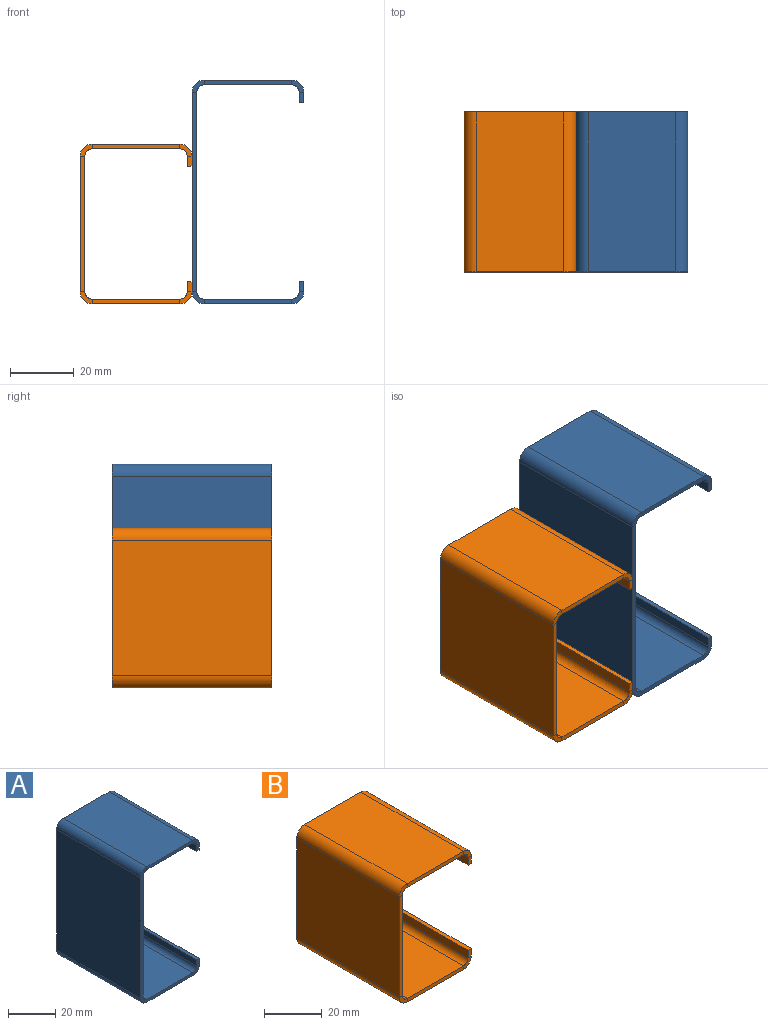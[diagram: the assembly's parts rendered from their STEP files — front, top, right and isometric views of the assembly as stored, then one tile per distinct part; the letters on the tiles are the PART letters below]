
ASSEMBLY  parts=2 mates=1
PART A: 38 faces, bbox 35x50x70 mm
  f0: plane 27.4x1.5mm, normal (0,1,0), area 41.1mm2, adj f2,f3,f26,f35
  f1: plane 27.4x1.5mm, normal (0,-1,0), area 41.1mm2, adj f2,f3,f25,f34
  f2: plane 50x27.4mm, normal (0,0,1), area 1370mm2, adj f0,f1,f28,f37
  f3: plane 50x27.4mm, normal (0,0,-1), area 1370mm2, adj f0,f1,f27,f36
  f4: plane 62.4x1.5mm, normal (0,1,0), area 93.6mm2, adj f6,f7,f22,f26
  f5: plane 62.4x1.5mm, normal (0,-1,0), area 93.6mm2, adj f6,f7,f21,f25
  f6: plane 62.4x50mm, normal (1,0,0), area 3120mm2, adj f4,f5,f24,f28
  f7: plane 62.4x50mm, normal (-1,0,0), area 3120mm2, adj f4,f5,f23,f27
  f8: plane 27.4x1.5mm, normal (0,1,0), area 41.1mm2, adj f10,f11,f18,f22
  f9: plane 27.4x1.5mm, normal (0,-1,0), area 41.1mm2, adj f10,f11,f17,f21
  f10: plane 50x27.4mm, normal (0,0,-1), area 1370mm2, adj f8,f9,f20,f24
  f11: plane 50x27.4mm, normal (0,0,1), area 1370mm2, adj f8,f9,f19,f23
  f12: plane 3.2x1.5mm, normal (0,1,0), area 4.8mm2, adj f13,f15,f16,f18
  f13: plane 50x1.5mm, normal (0,0,-1), area 75mm2, adj f12,f14,f15,f16
  f14: plane 3.2x1.5mm, normal (0,-1,0), area 4.8mm2, adj f13,f15,f16,f17
  f15: plane 50x3.2mm, normal (-1,0,0), area 160mm2, adj f12,f13,f14,f20
  f16: plane 50x3.2mm, normal (1,0,0), area 160mm2, adj f12,f13,f14,f19
  f17: plane 3.8x3.8mm, normal (0,-1,0), area 7.2mm2, adj f9,f14,f19,f20
  f18: plane 3.8x3.8mm, normal (0,1,0), area 7.2mm2, adj f8,f12,f19,f20
  f19: cylinder r=3.8mm len=50mm, axis (0,-1,0), area 298.5mm2, adj f11,f16,f17,f18
  f20: cylinder r=2.3mm len=50mm, axis (0,-1,0), area 180.6mm2, adj f10,f15,f17,f18
  f21: plane 3.8x3.8mm, normal (0,-1,0), area 7.2mm2, adj f5,f9,f23,f24
  f22: plane 3.8x3.8mm, normal (0,1,0), area 7.2mm2, adj f4,f8,f23,f24
  f23: cylinder r=3.8mm len=50mm, axis (0,-1,0), area 298.5mm2, adj f7,f11,f21,f22
  f24: cylinder r=2.3mm len=50mm, axis (0,-1,0), area 180.6mm2, adj f6,f10,f21,f22
  f25: plane 3.8x3.8mm, normal (0,-1,0), area 7.2mm2, adj f1,f5,f27,f28
  f26: plane 3.8x3.8mm, normal (0,1,0), area 7.2mm2, adj f0,f4,f27,f28
  f27: cylinder r=3.8mm len=50mm, axis (0,-1,0), area 298.5mm2, adj f3,f7,f25,f26
  f28: cylinder r=2.3mm len=50mm, axis (0,-1,0), area 180.6mm2, adj f2,f6,f25,f26
  f29: plane 3.2x1.5mm, normal (0,1,0), area 4.8mm2, adj f31,f32,f33,f35
  f30: plane 3.2x1.5mm, normal (0,-1,0), area 4.8mm2, adj f31,f32,f33,f34
  f31: plane 50x1.5mm, normal (0,0,1), area 75mm2, adj f29,f30,f32,f33
  f32: plane 50x3.2mm, normal (-1,0,0), area 160mm2, adj f29,f30,f31,f37
  f33: plane 50x3.2mm, normal (1,0,0), area 160mm2, adj f29,f30,f31,f36
  f34: plane 3.8x3.8mm, normal (0,-1,0), area 7.2mm2, adj f1,f30,f36,f37
  f35: plane 3.8x3.8mm, normal (0,1,0), area 7.2mm2, adj f0,f29,f36,f37
  f36: cylinder r=3.8mm len=50mm, axis (0,-1,0), area 298.5mm2, adj f3,f33,f34,f35
  f37: cylinder r=2.3mm len=50mm, axis (0,-1,0), area 180.6mm2, adj f2,f32,f34,f35
PART B: 38 faces, bbox 35x50x50 mm
  f0: plane 3.2x1.5mm, normal (0,1,0), area 4.8mm2, adj f2,f3,f4,f35
  f1: plane 3.2x1.5mm, normal (0,-1,0), area 4.8mm2, adj f2,f3,f4,f34
  f2: plane 50x1.5mm, normal (0,0,-1), area 75mm2, adj f0,f1,f3,f4
  f3: plane 50x3.2mm, normal (1,0,0), area 160mm2, adj f0,f1,f2,f36
  f4: plane 50x3.2mm, normal (-1,0,0), area 160mm2, adj f0,f1,f2,f37
  f5: plane 27.4x1.5mm, normal (0,1,0), area 41.1mm2, adj f7,f8,f31,f35
  f6: plane 27.4x1.5mm, normal (0,-1,0), area 41.1mm2, adj f7,f8,f30,f34
  f7: plane 50x27.4mm, normal (0,0,1), area 1370mm2, adj f5,f6,f32,f36
  f8: plane 50x27.4mm, normal (0,0,-1), area 1370mm2, adj f5,f6,f33,f37
  f9: plane 42.4x1.5mm, normal (0,1,0), area 63.6mm2, adj f11,f12,f27,f31
  f10: plane 42.4x1.5mm, normal (0,-1,0), area 63.6mm2, adj f11,f12,f26,f30
  f11: plane 50x42.4mm, normal (-1,0,0), area 2120mm2, adj f9,f10,f28,f32
  f12: plane 50x42.4mm, normal (1,0,0), area 2120mm2, adj f9,f10,f29,f33
  f13: plane 27.4x1.5mm, normal (0,1,0), area 41.1mm2, adj f15,f16,f23,f27
  f14: plane 27.4x1.5mm, normal (0,-1,0), area 41.1mm2, adj f15,f16,f22,f26
  f15: plane 50x27.4mm, normal (0,0,-1), area 1370mm2, adj f13,f14,f24,f28
  f16: plane 50x27.4mm, normal (0,0,1), area 1370mm2, adj f13,f14,f25,f29
  f17: plane 3.2x1.5mm, normal (0,1,0), area 4.8mm2, adj f18,f20,f21,f23
  f18: plane 50x1.5mm, normal (0,0,1), area 75mm2, adj f17,f19,f20,f21
  f19: plane 3.2x1.5mm, normal (0,-1,0), area 4.8mm2, adj f18,f20,f21,f22
  f20: plane 50x3.2mm, normal (1,0,0), area 160mm2, adj f17,f18,f19,f24
  f21: plane 50x3.2mm, normal (-1,0,0), area 160mm2, adj f17,f18,f19,f25
  f22: plane 3.8x3.8mm, normal (0,-1,0), area 7.2mm2, adj f14,f19,f24,f25
  f23: plane 3.8x3.8mm, normal (0,1,0), area 7.2mm2, adj f13,f17,f24,f25
  f24: cylinder r=3.8mm len=50mm, axis (0,-1,0), area 298.5mm2, adj f15,f20,f22,f23
  f25: cylinder r=2.3mm len=50mm, axis (0,-1,0), area 180.6mm2, adj f16,f21,f22,f23
  f26: plane 3.8x3.8mm, normal (0,-1,0), area 7.2mm2, adj f10,f14,f28,f29
  f27: plane 3.8x3.8mm, normal (0,1,0), area 7.2mm2, adj f9,f13,f28,f29
  f28: cylinder r=3.8mm len=50mm, axis (0,-1,0), area 298.5mm2, adj f11,f15,f26,f27
  f29: cylinder r=2.3mm len=50mm, axis (0,-1,0), area 180.6mm2, adj f12,f16,f26,f27
  f30: plane 3.8x3.8mm, normal (0,-1,0), area 7.2mm2, adj f6,f10,f32,f33
  f31: plane 3.8x3.8mm, normal (0,1,0), area 7.2mm2, adj f5,f9,f32,f33
  f32: cylinder r=3.8mm len=50mm, axis (0,-1,0), area 298.5mm2, adj f7,f11,f30,f31
  f33: cylinder r=2.3mm len=50mm, axis (0,-1,0), area 180.6mm2, adj f8,f12,f30,f31
  f34: plane 3.8x3.8mm, normal (0,-1,0), area 7.2mm2, adj f1,f6,f36,f37
  f35: plane 3.8x3.8mm, normal (0,1,0), area 7.2mm2, adj f0,f5,f36,f37
  f36: cylinder r=3.8mm len=50mm, axis (0,-1,0), area 298.5mm2, adj f3,f7,f34,f35
  f37: cylinder r=2.3mm len=50mm, axis (0,-1,0), area 180.6mm2, adj f4,f8,f34,f35
PLACE A t=(-15.16,17.81,2.35)mm
PLACE B t=(-50.16,17.81,-7.65)mm
MATE fastened B.f19 <-> A.f5  axis (0,-1,0) through (-32.66,-32.19,-28.85)mm
